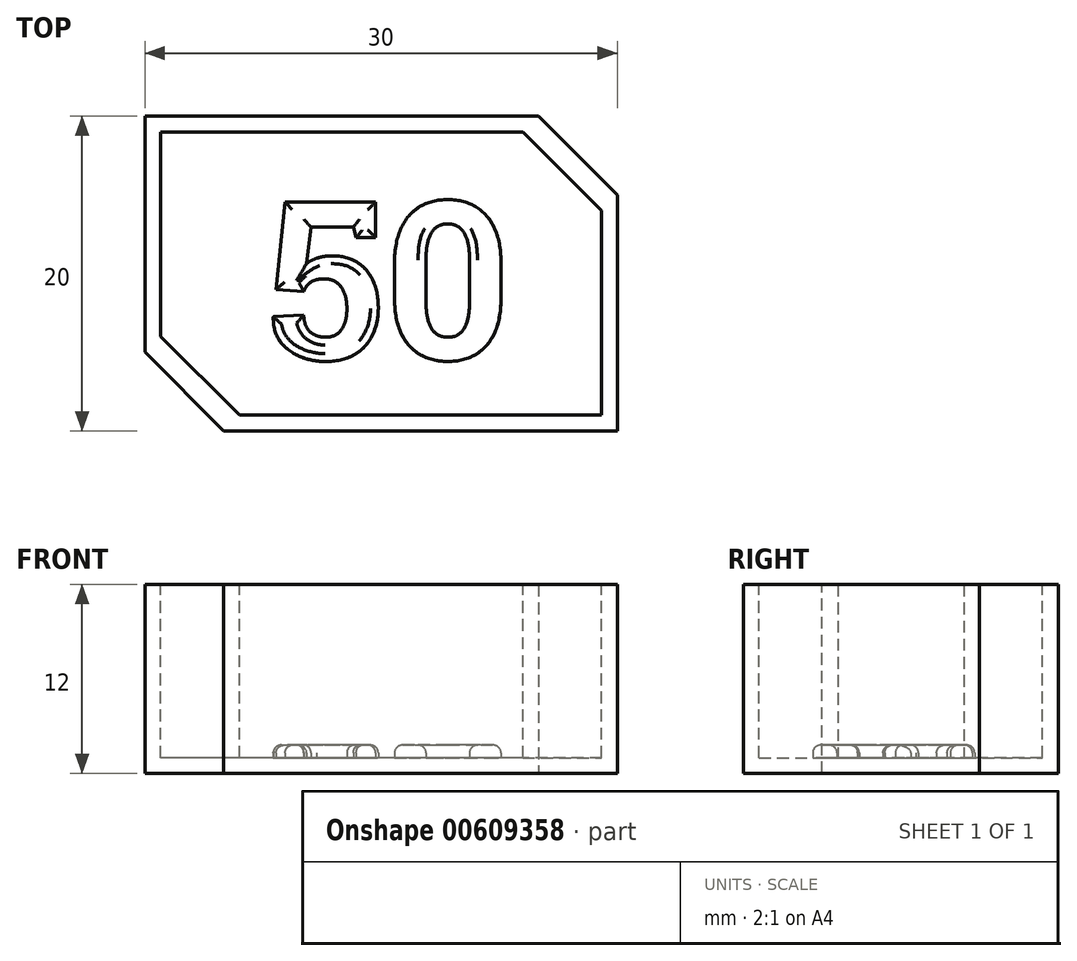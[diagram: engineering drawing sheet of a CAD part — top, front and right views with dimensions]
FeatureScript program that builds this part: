
annotation { "Feature Type Name" : "Feature", "Feature Type Description" : "" }
export const myFeature = defineFeature(function(context is Context, id is Id, definition is map)
    precondition{}
    {
        {
            var Q0;
            Q0=qCreatedBy(makeId("Top.planeOp"),FACE);
            var sketch = newSketch(context, id + "F0", { "sketchPlane" : qUnion([Q0])});
            skLineSegment(sketch, "E0.bottom", {"start": v(15, -10) * mm, "end": v(-15, -10) * mm});
            skLineSegment(sketch, "E0.top", {"start": v(15, 10) * mm, "end": v(-15, 10) * mm});
            skLineSegment(sketch, "E0.left", {"start": v(15, -10) * mm, "end": v(15, 10) * mm});
            skLineSegment(sketch, "E0.right", {"start": v(-15, -10) * mm, "end": v(-15, 10) * mm});
            skPoint(sketch, "E0.middle", {"position": v(0, 0) * mm});
            skSolve(sketch);
        }
        {
            var Q0;
            Q0=qSketchRegion(id+"F0",true);
            extrude(context, id + "F1", {"entities" : qUnion([Q0]), "depth" : 12 * mm, "offsetDistance" : 25 * mm});
        }
        {
            var Q0;
            Q0=makeQuery(id+"F1.opExtrude","CAP_FACE",FACE,{"disambiguationData":[OSD([sQuery(id+"F0.wireOp",EDGE,"E0.bottom"),sQuery(id+"F0.wireOp",EDGE,"E0.top"),sQuery(id+"F0.wireOp",EDGE,"E0.left"),sQuery(id+"F0.wireOp",EDGE,"E0.right")])],"isStart":false});
            var sketch = newSketch(context, id + "F2", { "sketchPlane" : qUnion([Q0])});
            skLineSegment(sketch, "E1.bottom", {"start": v(14, -9) * mm, "end": v(-14, -9) * mm});
            skLineSegment(sketch, "E1.top", {"start": v(14, 9) * mm, "end": v(-14, 9) * mm});
            skLineSegment(sketch, "E1.left", {"start": v(14, -9) * mm, "end": v(14, 9) * mm});
            skLineSegment(sketch, "E1.right", {"start": v(-14, -9) * mm, "end": v(-14, 9) * mm});
            skPoint(sketch, "E1.middle", {"position": v(0, 0) * mm});
            skSolve(sketch);
        }
        {
            var Q0;
            Q0=qSketchRegion(id+"F2",true);
            extrude(context, id + "F3", {"entities" : qUnion([Q0]), "operationType" : NewBodyOperationType.REMOVE, "oppositeDirection" : true, "depth" : 11 * mm, "offsetDistance" : 25 * mm});
        }
        {
            var Q0;
            Q0=makeQuery(id+"F3.boolean.opBoolean","COPY",EDGE,{"derivedFrom":makeQuery(id+"F3.opExtrude","SWEPT_EDGE",EDGE,{"disambiguationData":[OSD([sQuery(id+"F2.wireOp",EDGE,"E1.top"),sQuery(id+"F2.wireOp",EDGE,"E1.left")])]})});
            var Q1;
            Q1=makeQuery(id+"F3.boolean.opBoolean","COPY",EDGE,{"derivedFrom":makeQuery(id+"F3.opExtrude","SWEPT_EDGE",EDGE,{"disambiguationData":[OSD([sQuery(id+"F2.wireOp",EDGE,"E1.bottom"),sQuery(id+"F2.wireOp",EDGE,"E1.right")])]})});
            var Q2;
            Q2=makeQuery(id+"F1.opExtrude","SWEPT_EDGE",EDGE,{"disambiguationData":[OSD([sQuery(id+"F0.wireOp",EDGE,"E0.top"),sQuery(id+"F0.wireOp",EDGE,"E0.left")])]});
            var Q3;
            Q3=makeQuery(id+"F1.opExtrude","SWEPT_EDGE",EDGE,{"disambiguationData":[OSD([sQuery(id+"F0.wireOp",EDGE,"E0.bottom"),sQuery(id+"F0.wireOp",EDGE,"E0.right")])]});
            chamfer(context, id + "F4", {"entities" : qUnion([Q0, Q1, Q2, Q3]), "width" : 5 * mm, "tangentPropagation" : true});
        }
        {
            var Q0;
            Q0=makeQuery(id+"F3.boolean.opBoolean","COPY",FACE,{"derivedFrom":makeQuery(id+"F3.opExtrude","CAP_FACE",FACE,{"disambiguationData":[OSD([sQuery(id+"F2.wireOp",EDGE,"E1.bottom"),sQuery(id+"F2.wireOp",EDGE,"E1.top"),sQuery(id+"F2.wireOp",EDGE,"E1.left"),sQuery(id+"F2.wireOp",EDGE,"E1.right")])],"isStart":false})});
            var sketch = newSketch(context, id + "F5", { "sketchPlane" : qUnion([Q0])});
            skSolve(sketch);
        }
        {
            var Q0;
            {var subQ1=sQuery(id+"F2.wireOp",EDGE,"E1.top");Q0=makeQuery(id+"F5.imprint","IMPRINT",FACE,{"disambiguationData":[TD([[makeQuery(id+"F5.imprint","IMPRINT",EDGE,{"derivedFrom":makeQuery(id+"F3.boolean.opBoolean","COPY",EDGE,{"derivedFrom":makeQuery(id+"F3.opExtrude","CAP_EDGE",EDGE,{"disambiguationData":[OSD([subQ1])],"isStart":false})})}),1.0]])]});}
            var sketch = newSketch(context, id + "F6", { "sketchPlane" : qUnion([Q0])});
            skText(sketch, "E2", { "text": "50", "fontName": "RobotoSlab-Bold.ttf"});
            const initialGuessF6  = {"E2": [-0.00731, -0.00544, 1, 0, 0.01012]};
            skSetInitialGuess(sketch, initialGuessF6);
            skSolve(sketch);
        }
        {
            var Q0;
            Q0=qSketchRegion(id+"F6",true);
            extrude(context, id + "F7", {"entities" : qUnion([Q0]), "operationType" : NewBodyOperationType.ADD, "depth" : 0.8 * mm, "offsetDistance" : 25 * mm});
        }
        {
            var Q0;
            Q0=makeQuery(id+"F7.opExtrude","CAP_EDGE",EDGE,{"disambiguationData":[OSD([sQuery(id+"F6.wireOp",EDGE,"E2.sketch_text.stroke-23")])],"isStart":false});
            var Q1;
            Q1=makeQuery(id+"F7.opExtrude","CAP_EDGE",EDGE,{"disambiguationData":[OSD([sQuery(id+"F6.wireOp",EDGE,"E2.sketch_text.stroke-22")])],"isStart":false});
            var Q2;
            Q2=makeQuery(id+"F7.opExtrude","CAP_EDGE",EDGE,{"disambiguationData":[OSD([sQuery(id+"F6.wireOp",EDGE,"E2.sketch_text.stroke-18")])],"isStart":false});
            var Q3;
            Q3=makeQuery(id+"F7.opExtrude","CAP_EDGE",EDGE,{"disambiguationData":[OSD([sQuery(id+"F6.wireOp",EDGE,"E2.sketch_text.stroke-24")])],"isStart":false});
            var Q4;
            Q4=makeQuery(id+"F7.opExtrude","CAP_EDGE",EDGE,{"disambiguationData":[OSD([sQuery(id+"F6.wireOp",EDGE,"E2.sketch_text.stroke-1")])],"isStart":false});
            var Q5;
            Q5=makeQuery(id+"F7.opExtrude","CAP_EDGE",EDGE,{"disambiguationData":[OSD([sQuery(id+"F6.wireOp",EDGE,"E2.sketch_text.stroke-25")])],"isStart":false});
            var Q6;
            Q6=makeQuery(id+"F7.opExtrude","CAP_EDGE",EDGE,{"disambiguationData":[OSD([sQuery(id+"F6.wireOp",EDGE,"E2.sketch_text.stroke-0")])],"isStart":false});
            var Q7;
            Q7=makeQuery(id+"F7.opExtrude","CAP_EDGE",EDGE,{"disambiguationData":[OSD([sQuery(id+"F6.wireOp",EDGE,"E2.sketch_text.stroke-2")])],"isStart":false});
            var Q8;
            Q8=makeQuery(id+"F7.opExtrude","CAP_EDGE",EDGE,{"disambiguationData":[OSD([sQuery(id+"F6.wireOp",EDGE,"E2.sketch_text.stroke-5")])],"isStart":false});
            var Q9;
            Q9=makeQuery(id+"F7.opExtrude","CAP_EDGE",EDGE,{"disambiguationData":[OSD([sQuery(id+"F6.wireOp",EDGE,"E2.sketch_text.stroke-4")])],"isStart":false});
            var Q10;
            Q10=makeQuery(id+"F7.opExtrude","CAP_EDGE",EDGE,{"disambiguationData":[OSD([sQuery(id+"F6.wireOp",EDGE,"E2.sketch_text.stroke-12")])],"isStart":false});
            var Q11;
            Q11=makeQuery(id+"F7.opExtrude","CAP_EDGE",EDGE,{"disambiguationData":[OSD([sQuery(id+"F6.wireOp",EDGE,"E2.sketch_text.stroke-21")])],"isStart":false});
            var Q12;
            Q12=makeQuery(id+"F7.opExtrude","CAP_EDGE",EDGE,{"disambiguationData":[OSD([sQuery(id+"F6.wireOp",EDGE,"E2.sketch_text.stroke-32")])],"isStart":false});
            var Q13;
            Q13=makeQuery(id+"F7.opExtrude","CAP_EDGE",EDGE,{"disambiguationData":[OSD([sQuery(id+"F6.wireOp",EDGE,"E2.sketch_text.stroke-38")])],"isStart":false});
            fillet(context, id + "F8", {"entities" : qUnion([Q0, Q1, Q2, Q3, Q4, Q5, Q6, Q7, Q8, Q9, Q10, Q11, Q12, Q13]), "radius" : 0.5 * mm, "tangentPropagation" : true, "allowEdgeOverflow" : false});
        }
    });
